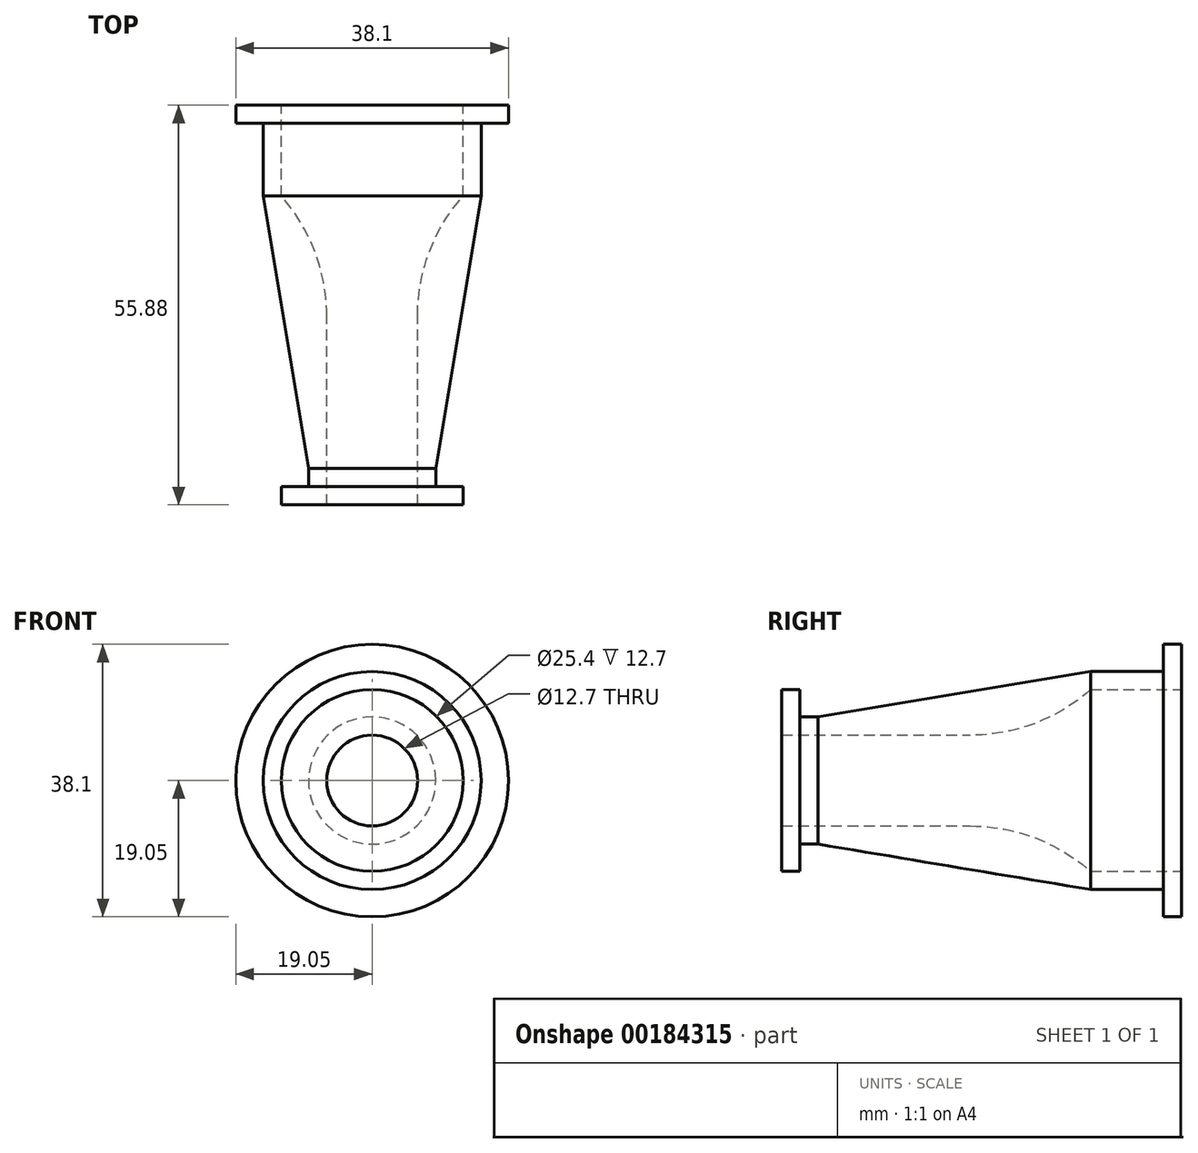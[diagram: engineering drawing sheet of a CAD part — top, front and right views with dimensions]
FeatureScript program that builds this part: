
annotation { "Feature Type Name" : "Feature", "Feature Type Description" : "" }
export const myFeature = defineFeature(function(context is Context, id is Id, definition is map)
    precondition{}
    {
        {
            var Q0;
            Q0=qCreatedBy(makeId("Front.planeOp"),FACE);
            var sketch = newSketch(context, id + "F0", { "sketchPlane" : qUnion([Q0])});
            skCircle(sketch, "E0", {"center": v(0, 0) * mm, "radius": 19.05 * mm});
            skCircle(sketch, "E1", {"center": v(0, 0) * mm, "radius": 15.24 * mm});
            skCircle(sketch, "E2", {"center": v(0, 0) * mm, "radius": 12.7 * mm});
            skSolve(sketch);
        }
        {
            var Q0;
            Q0=makeQuery(id+"F0.imprint","IMPRINT",FACE,{"disambiguationData":[TD([[makeQuery(id+"F0.imprint","IMPRINT",EDGE,{"derivedFrom":sQuery(id+"F0.wireOp",EDGE,"E1")}),1.0]])]});
            extrude(context, id + "F1", {"entities" : qUnion([Q0]), "depth" : 12.7 * mm});
        }
        {
            var Q0;
            Q0=makeQuery(id+"F0.imprint","IMPRINT",FACE,{"disambiguationData":[TD([[makeQuery(id+"F0.imprint","IMPRINT",EDGE,{"derivedFrom":sQuery(id+"F0.wireOp",EDGE,"E0")}),1.0]])]});
            extrude(context, id + "F2", {"entities" : qUnion([Q0]), "operationType" : NewBodyOperationType.ADD, "depth" : 2.54 * mm});
        }
        {
            var Q0;
            Q0=qCreatedBy(makeId("Front.planeOp"),FACE);
            cPlane(context, id + "F3", {"entities" : qUnion([Q0]), "cplaneType" : CPlaneType.OFFSET, "offset" : 50.8 * mm, "width" : 152.4 * mm, "height" : 152.4 * mm});
        }
        {
            var Q0;
            Q0=qCreatedBy(id+"F3.planeOp",FACE);
            var sketch = newSketch(context, id + "F4", { "sketchPlane" : qUnion([Q0])});
            skCircle(sketch, "E3", {"center": v(0, 0) * mm, "radius": 8.9 * mm});
            skSolve(sketch);
        }
        {
            var Q0;
            Q0=makeQuery(id+"F1.opExtrude","CAP_FACE",FACE,{"disambiguationData":[OSD([sQuery(id+"F0.wireOp",EDGE,"E1"),sQuery(id+"F0.wireOp",EDGE,"E2")])],"isStart":false});
            var sketch = newSketch(context, id + "F5", { "sketchPlane" : qUnion([Q0])});
            skCircle(sketch, "E4", {"center": v(0, 0) * mm, "radius": 15.24 * mm});
            skSolve(sketch);
        }
        {
            var Q1;
            Q1=qSketchRegion(id+"F5",true);
            var Q2;
            Q2=makeQuery(id+"F4.imprint","IMPRINT",FACE,{"disambiguationData":[TD([[makeQuery(id+"F4.imprint","IMPRINT",EDGE,{"derivedFrom":sQuery(id+"F4.wireOp",EDGE,"E3")}),1.0]])]});
            loft(context, id + "F6", {"operationType" : NewBodyOperationType.ADD, "sheetProfilesArray" : [{ "sheetProfileEntities" : qUnion([Q1]) }, { "sheetProfileEntities" : qUnion([Q2]) }]});
        }
        {
            var Q0;
            Q0=makeQuery(id+"F6.opLoft","CAP_FACE",FACE,{"disambiguationData":[OSD([makeQuery(id+"F4.imprint","IMPRINT",FACE,{"disambiguationData":[TD([[makeQuery(id+"F4.imprint","IMPRINT",EDGE,{"derivedFrom":sQuery(id+"F4.wireOp",EDGE,"E3")}),1.0]])]})])],"isStart":true});
            var sketch = newSketch(context, id + "F7", { "sketchPlane" : qUnion([Q0])});
            skCircle(sketch, "E5", {"center": v(0, 0) * mm, "radius": 6.35 * mm});
            skCircle(sketch, "E6", {"center": v(0, 0) * mm, "radius": 8.9 * mm});
            skSolve(sketch);
        }
        {
            var Q0;
            Q0 = qSketchRegion(id + "F7", true);
            extrude(context, id + "F8", {"entities" : qUnion([Q0]), "operationType" : NewBodyOperationType.ADD, "depth" : 2.54 * mm});
        }
        {
            var Q0;
            Q0=makeQuery(id+"F8.opExtrude","CAP_FACE",FACE,{"disambiguationData":[OSD([sQuery(id+"F7.wireOp",EDGE,"E5"),sQuery(id+"F7.wireOp",EDGE,"E6")])],"isStart":false});
            var sketch = newSketch(context, id + "F9", { "sketchPlane" : qUnion([Q0])});
            skCircle(sketch, "E7", {"center": v(0, 0) * mm, "radius": 12.7 * mm});
            skCircle(sketch, "E8", {"center": v(0, 0) * mm, "radius": 6.35 * mm});
            skSolve(sketch);
        }
        {
            var Q0;
            Q0 = qSketchRegion(id + "F9", true);
            extrude(context, id + "F10", {"entities" : qUnion([Q0]), "operationType" : NewBodyOperationType.ADD, "depth" : 2.54 * mm});
        }
        {
            var Q0;
            Q0=makeQuery(id+"F6.opLoft","CAP_FACE",FACE,{"disambiguationData":[OSD([makeQuery(id+"F4.imprint","IMPRINT",FACE,{"disambiguationData":[TD([[makeQuery(id+"F4.imprint","IMPRINT",EDGE,{"derivedFrom":sQuery(id+"F4.wireOp",EDGE,"E3")}),1.0]])]})])],"isStart":true});
            extrude(context, id + "F11", {"entities" : qUnion([Q0]), "operationType" : NewBodyOperationType.REMOVE, "oppositeDirection" : true, "depth" : 41.4 * mm});
        }
        {
            var Q0;
            Q0=makeQuery(id+"F11.boolean.opBoolean","INTERSECT",EDGE,{"derivedFrom":[makeQuery(id+"F6.opLoft","CAP_FACE",FACE,{"disambiguationData":[OSD([makeQuery(id+"F5.imprint","IMPRINT",FACE,{"disambiguationData":[TD([[makeQuery(id+"F5.imprint","IMPRINT",EDGE,{"derivedFrom":makeQuery(id+"F1.opExtrude","CAP_EDGE",EDGE,{"disambiguationData":[OSD([sQuery(id+"F0.wireOp",EDGE,"E2")])],"isStart":false})}),1.0]])]})])],"isStart":true}),makeQuery(id+"F11.opExtrude","SWEPT_FACE",FACE,{"disambiguationData":[OSD([sQuery(id+"F7.wireOp",EDGE,"E5")])]})]});
            fillet(context, id + "F12", {"entities" : qUnion([Q0]), "radius" : 25.4 * mm, "tangentPropagation" : true, "allowEdgeOverflow" : false});
        }
    });
